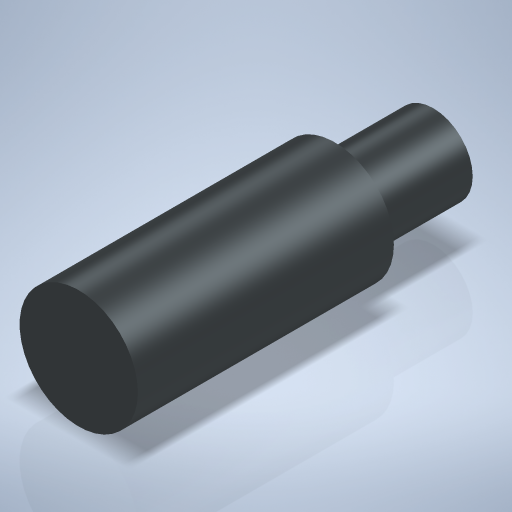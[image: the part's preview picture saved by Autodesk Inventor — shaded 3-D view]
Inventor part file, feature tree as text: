
AUTODESK INVENTOR PART (.ipt)
format: ipt  version: 2024 (Build 280153000, 153)  size: 266,240 bytes
history: native  units: mm
features: revolve x1, sketch x1
ambient origin geometry x8: Origin, YZ Plane, XZ Plane, XY Plane, X Axis, Y Axis, Z Axis, Center Point
bodies: Volumenkörper1 (feature_tree)
feature tree (2):
  revolve  "Umdrehung1"
  sketch  "Skizze1"  dims[d0=54.0mm d1=18.0mm d2=39.0mm d3=90.0deg d4=12.0mm]
